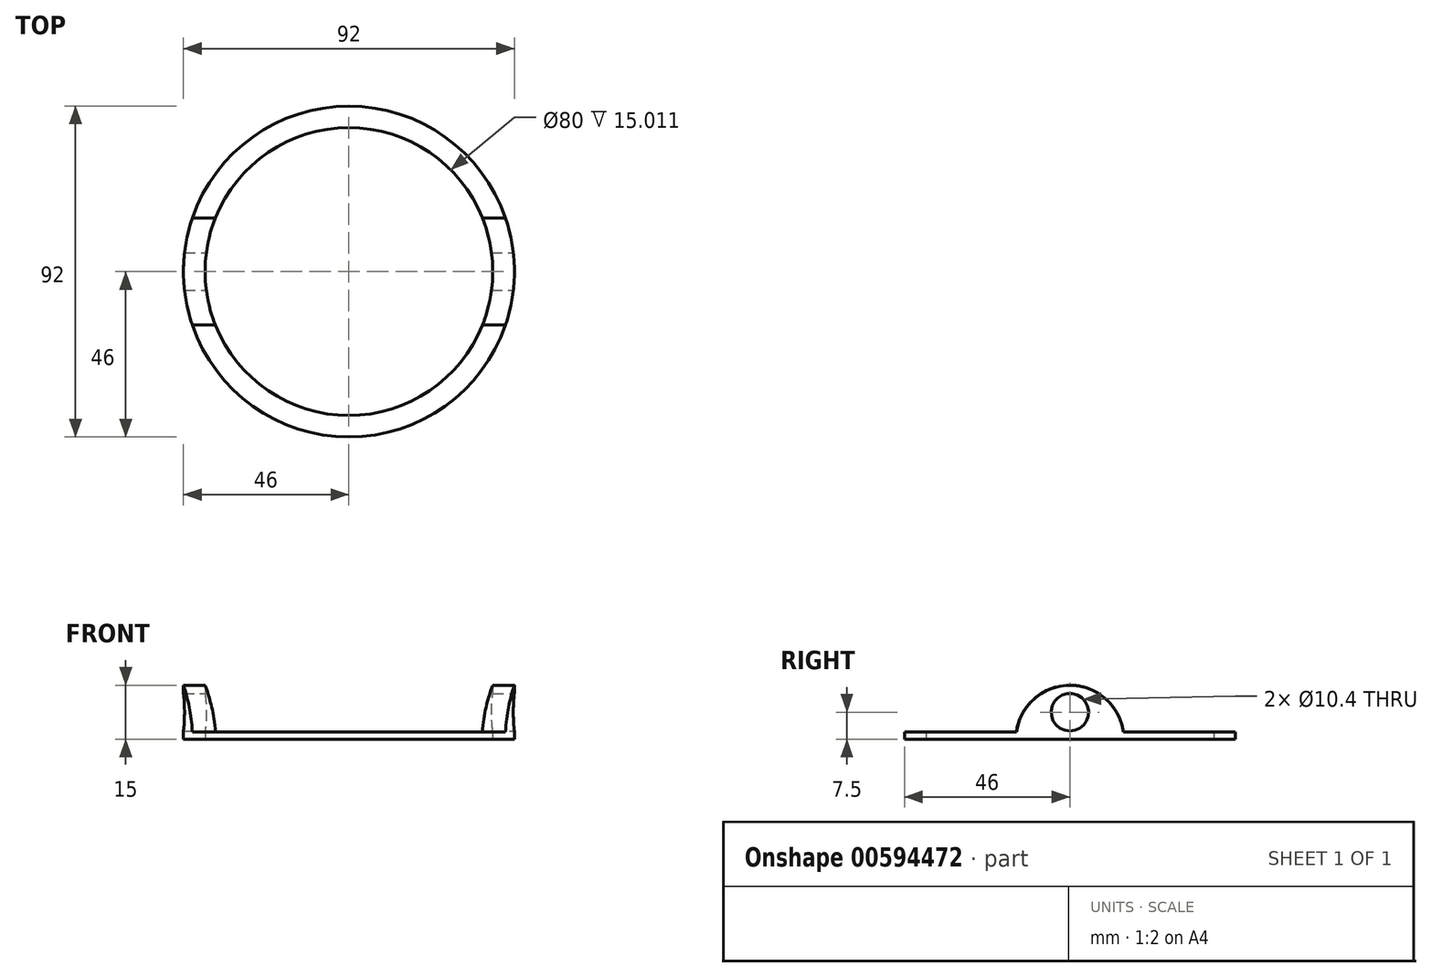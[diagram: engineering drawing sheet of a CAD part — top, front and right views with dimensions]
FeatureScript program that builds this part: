
annotation { "Feature Type Name" : "Feature", "Feature Type Description" : "" }
export const myFeature = defineFeature(function(context is Context, id is Id, definition is map)
    precondition{}
    {
        {
            var Q0;
            Q0=qCreatedBy(makeId("Top.planeOp"),FACE);
            var sketch = newSketch(context, id + "F0", { "sketchPlane" : qUnion([Q0])});
            skCircle(sketch, "E0", {"center": v(0, 0) * mm, "radius": 46 * mm});
            skCircle(sketch, "E1", {"center": v(0, 0) * mm, "radius": 40 * mm});
            skSolve(sketch);
        }
        {
            var Q0;
            Q0=qSketchRegion(id+"F0",true);
            extrude(context, id + "F1", {"entities" : qUnion([Q0]), "depth" : 2 * mm});
        }
        {
            var Q0;
            Q0=qCreatedBy(makeId("Right.planeOp"),FACE);
            var sketch = newSketch(context, id + "F2", { "sketchPlane" : qUnion([Q0])});
            skLineSegment(sketch, "E2.0", {"start": v(-40, 0) * mm, "end": v(40, 0) * mm});
            skArc(sketch, "E3", {"start": v(-15, 0) * mm, "mid": v(0, -15) * mm, "end": v(15, 0) * mm, "construction": true});
            skArc(sketch, "E4", {"start": v(15, 0) * mm, "mid": v(0, 15) * mm, "end": v(-15, 0) * mm});
            skLineSegment(sketch, "E5", {"start": v(-15, 0) * mm, "end": v(15, 0) * mm});
            skSolve(sketch);
        }
        {
            var Q0;
            Q0=qSketchRegion(id+"F2",true);
            var Q1;
            Q1=qConstructionFilter(qBodyType(qCreatedBy(id+"F2",EDGE),BodyType.WIRE),ConstructionObject.NO);
            var Q2;
            Q2=makeQuery(id+"F1.opExtrude","SWEPT_FACE",FACE,{"disambiguationData":[OSD([sQuery(id+"F0.wireOp",EDGE,"E0")])]});
            var Q3;
            Q3=makeQuery(id+"F1.opExtrude","SWEPT_FACE",FACE,{"disambiguationData":[OSD([sQuery(id+"F0.wireOp",EDGE,"E0")])]});
            extrude(context, id + "F3", {"entities" : qUnion([Q0]), "operationType" : NewBodyOperationType.ADD, "surfaceEntities" : qUnion([Q1]), "endBound" : BoundingType.UP_TO_SURFACE, "endBoundEntityFace" : qUnion([Q2]), "depth" : 25 * mm, "hasSecondDirection" : true, "secondDirectionBound" : SecondDirectionBoundingType.UP_TO_SURFACE, "secondDirectionOppositeDirection" : true, "secondDirectionBoundEntityFace" : qUnion([Q3]), "secondDirectionDepth" : 25 * mm});
        }
        {
            var Q0;
            Q0=qCreatedBy(makeId("Top.planeOp"),FACE);
            var sketch = newSketch(context, id + "F4", { "sketchPlane" : qUnion([Q0])});
            skCircle(sketch, "E6.0", {"center": v(0, 0) * mm, "radius": 46 * mm});
            skCircle(sketch, "E7", {"center": v(0, 0) * mm, "radius": 51 * mm});
            skSolve(sketch);
        }
        {
            var Q0;
            Q0=qSketchRegion(id+"F4",true);
            extrude(context, id + "F5", {"entities" : qUnion([Q0]), "operationType" : NewBodyOperationType.REMOVE, "endBound" : BoundingType.THROUGH_ALL, "depth" : 25 * mm});
        }
        {
            var Q0;
            Q0=qCreatedBy(makeId("Top.planeOp"),FACE);
            var sketch = newSketch(context, id + "F6", { "sketchPlane" : qUnion([Q0])});
            skCircle(sketch, "E8.0", {"center": v(0, 0) * mm, "radius": 40 * mm});
            skSolve(sketch);
        }
        {
            var Q0;
            Q0=qSketchRegion(id+"F6",true);
            extrude(context, id + "F7", {"entities" : qUnion([Q0]), "operationType" : NewBodyOperationType.REMOVE, "endBound" : BoundingType.THROUGH_ALL, "depth" : 25 * mm});
        }
        {
            var Q0;
            Q0=qCreatedBy(makeId("Right.planeOp"),FACE);
            var sketch = newSketch(context, id + "F8", { "sketchPlane" : qUnion([Q0])});
            skArc(sketch, "E9.0", {"start": v(-14.87, 2) * mm, "mid": v(0, 15) * mm, "end": v(14.87, 2) * mm, "construction": true});
            skLineSegment(sketch, "E10.0", {"start": v(-40, 0) * mm, "end": v(40, 0) * mm});
            skLineSegment(sketch, "E11", {"start": v(0, 15) * mm, "end": v(0, 0) * mm, "construction": true});
            skCircle(sketch, "E12", {"center": v(0, 7.5) * mm, "radius": 5.2 * mm});
            skSolve(sketch);
        }
        {
            var Q0;
            Q0=qSketchRegion(id+"F8",true);
            var Q1;
            Q1=qConstructionFilter(qBodyType(qCreatedBy(id+"F8",EDGE),BodyType.WIRE),ConstructionObject.NO);
            extrude(context, id + "F9", {"entities" : qUnion([Q0]), "operationType" : NewBodyOperationType.REMOVE, "surfaceEntities" : qUnion([Q1]), "endBound" : BoundingType.THROUGH_ALL, "oppositeDirection" : true, "depth" : 25 * mm, "hasSecondDirection" : true, "secondDirectionBound" : SecondDirectionBoundingType.THROUGH_ALL, "secondDirectionOppositeDirection" : false, "secondDirectionDepth" : 25 * mm});
        }
    });
